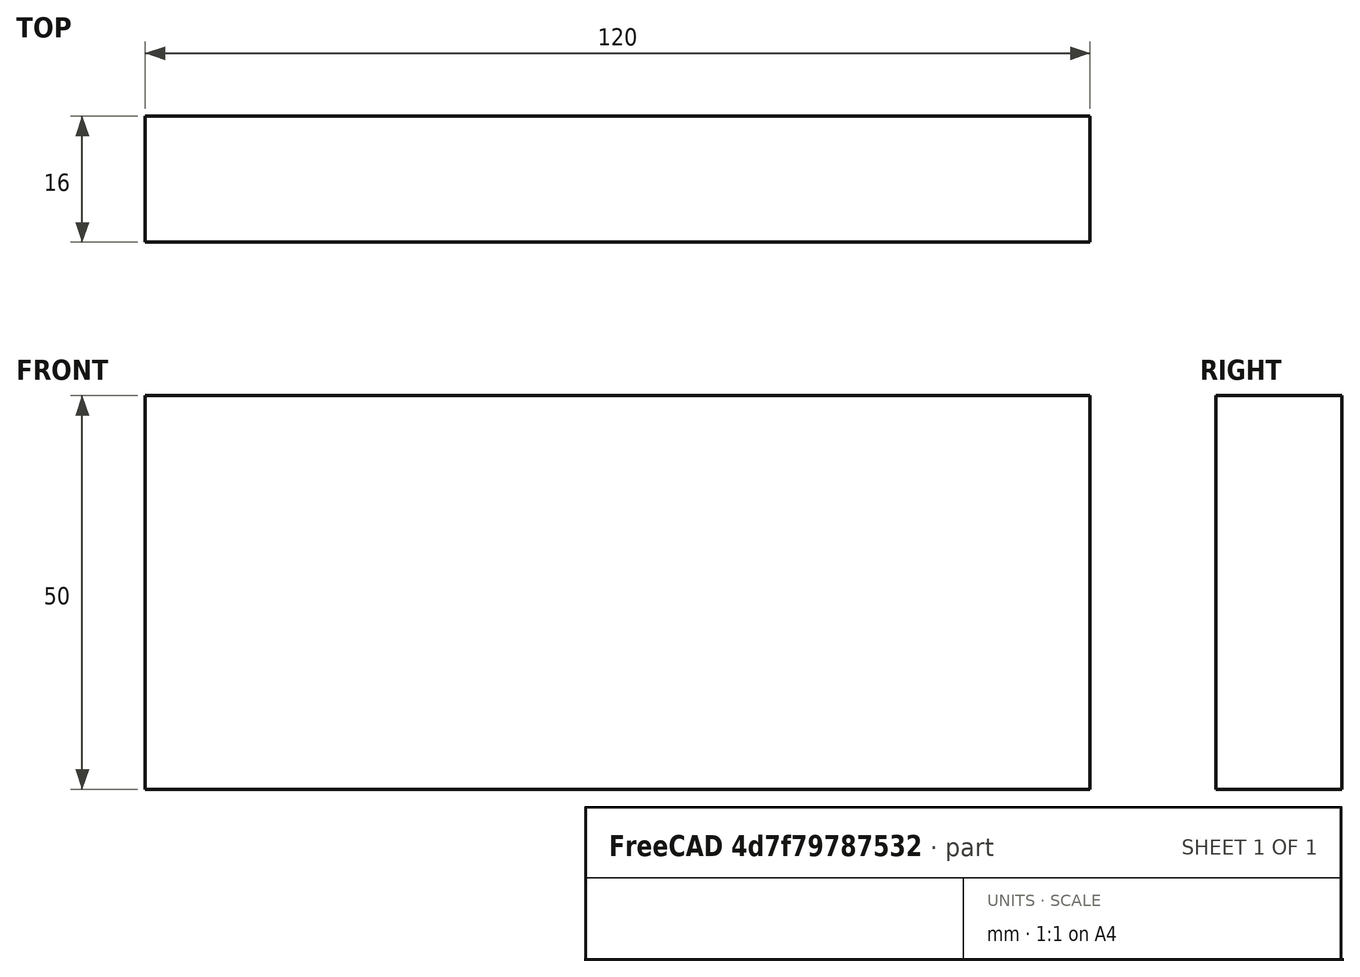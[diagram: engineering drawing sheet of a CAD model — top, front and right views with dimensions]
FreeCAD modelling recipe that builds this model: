
FCSTD DOCUMENT  (FreeCAD 0.15R4671 (Git))
Label: Flat Bar 120x16 EN10058 S235JR
License: All rights reserved
LicenseURL: http://en.wikipedia.org/wiki/All_rights_reserved
objects: Sketcher::SketchObject×1, Part::Extrusion×1
note: 2 computed .brp shape members not serialized (recipe doc carries the construction recipe); baked Part::Feature solids carry a one-line shape summary decoded from their .brp

FEATURE [Sketcher::SketchObject] Sketch
  sketch-geometry (4):
    g0: LineSegment StartX=-60 StartY=-8 StartZ=0 EndX=60 EndY=-8 EndZ=0
    g1: LineSegment StartX=60 StartY=-8 StartZ=0 EndX=60 EndY=8 EndZ=0
    g2: LineSegment StartX=60 StartY=8 StartZ=0 EndX=-60 EndY=8 EndZ=0
    g3: LineSegment StartX=-60 StartY=8 StartZ=0 EndX=-60 EndY=-8 EndZ=0
  constraints (12):
    c: Coincident(g0,g1)
    c: Coincident(g1,g2)
    c: Coincident(g2,g3)
    c: Coincident(g3,g0)
    c: Horizontal(g0)
    c: Horizontal(g2)
    c: Vertical(g1)
    c: Vertical(g3)
    c: Symmetric(g1,g2,g-2)
    c: Symmetric(g0,g1,g-1)
    c: DistanceY(g1) = 16
    c: DistanceX(g0) = 120
FEATURE [Part::Extrusion] Extrude  label="Flat Bar 120x16 EN10058 S235JR"
  Base = -> Sketch
  Dir = (0,0,50)
  Solid = true
